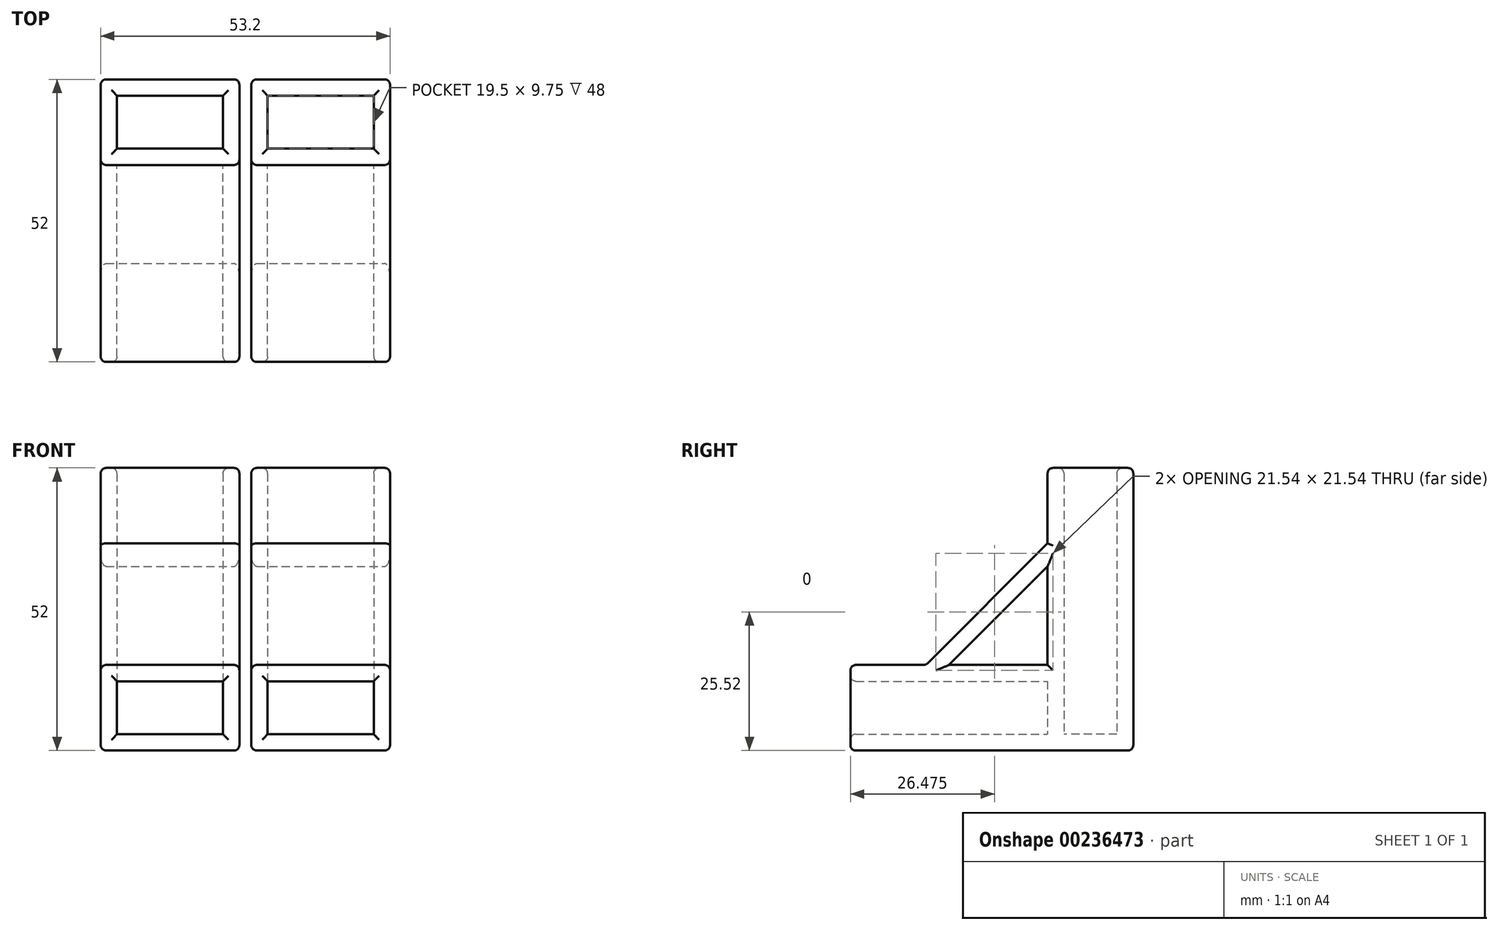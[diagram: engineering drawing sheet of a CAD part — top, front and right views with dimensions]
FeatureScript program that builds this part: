
annotation { "Feature Type Name" : "Feature", "Feature Type Description" : "" }
export const myFeature = defineFeature(function(context is Context, id is Id, definition is map)
    precondition{}
    {
        {
            var Q0;
            Q0=qCreatedBy(makeId("Top.planeOp"),FACE);
            var sketch = newSketch(context, id + "F0", { "sketchPlane" : qUnion([Q0])});
            skLineSegment(sketch, "E0.bottom", {"start": v(-9.75, 4.88) * mm, "end": v(9.75, 4.88) * mm});
            skLineSegment(sketch, "E0.top", {"start": v(-9.75, -4.88) * mm, "end": v(9.75, -4.88) * mm});
            skLineSegment(sketch, "E0.left", {"start": v(-9.75, 4.88) * mm, "end": v(-9.75, -4.88) * mm});
            skLineSegment(sketch, "E0.right", {"start": v(9.75, 4.88) * mm, "end": v(9.75, -4.88) * mm});
            skPoint(sketch, "E0.middle", {"position": v(0, 0) * mm});
            skLineSegment(sketch, "E1.0", {"start": v(-12.75, 7.88) * mm, "end": v(12.75, 7.88) * mm});
            skLineSegment(sketch, "E1.1", {"start": v(-12.75, 7.88) * mm, "end": v(-12.75, -7.88) * mm});
            skLineSegment(sketch, "E1.2", {"start": v(-12.75, -7.88) * mm, "end": v(12.75, -7.88) * mm});
            skLineSegment(sketch, "E1.3", {"start": v(12.75, 7.88) * mm, "end": v(12.75, -7.88) * mm});
            skSolve(sketch);
        }
        {
            var Q0;
            Q0=makeQuery(id+"F0.imprint","IMPRINT",FACE,{"disambiguationData":[TD([[makeQuery(id+"F0.imprint","IMPRINT",EDGE,{"derivedFrom":sQuery(id+"F0.wireOp",EDGE,"E0.bottom")}),1.0]])]});
            extrude(context, id + "F1", {"entities" : qUnion([Q0]), "depth" : 52 * mm, "offsetDistance" : 25 * mm});
        }
        {
            var Q0;
            Q0=makeQuery(id+"F1.opExtrude","SWEPT_FACE",FACE,{"disambiguationData":[OSD([sQuery(id+"F0.wireOp",EDGE,"E1.2")])]});
            var sketch = newSketch(context, id + "F2", { "sketchPlane" : qUnion([Q0])});
            skPoint(sketch, "E2", {"position": v(12.75, 3) * mm});
            skPoint(sketch, "E3", {"position": v(-12.75, 3) * mm});
            skPoint(sketch, "E4", {"position": v(12.75, 12.75) * mm});
            skPoint(sketch, "E5", {"position": v(-12.75, 12.75) * mm});
            skPoint(sketch, "E6", {"position": v(12.75, 15.75) * mm});
            skPoint(sketch, "E7", {"position": v(-12.75, 15.75) * mm});
            skPoint(sketch, "E8", {"position": v(9.75, 0) * mm});
            skPoint(sketch, "E9", {"position": v(9.75, 3) * mm});
            skPoint(sketch, "E10", {"position": v(9.75, 12.75) * mm});
            skPoint(sketch, "E11", {"position": v(9.75, 15.75) * mm});
            skPoint(sketch, "E12", {"position": v(-9.75, 0) * mm});
            skPoint(sketch, "E13", {"position": v(-9.75, 3) * mm});
            skPoint(sketch, "E14", {"position": v(-9.75, 12.75) * mm});
            skPoint(sketch, "E15", {"position": v(-9.75, 15.75) * mm});
            skLineSegment(sketch, "E16", {"start": v(12.75, 15.75) * mm, "end": v(-12.75, 15.75) * mm});
            skLineSegment(sketch, "E17", {"start": v(12.75, 15.75) * mm, "end": v(12.75, 0) * mm});
            skLineSegment(sketch, "E18", {"start": v(12.75, 0) * mm, "end": v(-12.75, 0) * mm});
            skLineSegment(sketch, "E19", {"start": v(-12.75, 0) * mm, "end": v(-12.75, 15.75) * mm});
            skLineSegment(sketch, "E20", {"start": v(9.75, 12.75) * mm, "end": v(9.75, 3) * mm});
            skLineSegment(sketch, "E21", {"start": v(-9.75, 3) * mm, "end": v(9.75, 3) * mm});
            skLineSegment(sketch, "E22", {"start": v(-9.75, 3) * mm, "end": v(-9.75, 12.75) * mm});
            skLineSegment(sketch, "E23", {"start": v(-9.75, 12.75) * mm, "end": v(9.75, 12.75) * mm});
            skSolve(sketch);
        }
        {
            var Q0;
            Q0=makeQuery(id+"F2.imprint","IMPRINT",FACE,{"disambiguationData":[TD([[makeQuery(id+"F2.imprint","IMPRINT",EDGE,{"derivedFrom":sQuery(id+"F2.wireOp",EDGE,"E16")}),1.0]])]});
            extrude(context, id + "F3", {"entities" : qUnion([Q0]), "operationType" : NewBodyOperationType.ADD, "depth" : 36.25 * mm, "offsetDistance" : 25 * mm});
        }
        {
            var Q0;
            Q0=makeQuery(id+"F0.imprint","IMPRINT",FACE,{"disambiguationData":[TD([[makeQuery(id+"F0.imprint","IMPRINT",EDGE,{"derivedFrom":sQuery(id+"F0.wireOp",EDGE,"E0.bottom")}),-1.0]])]});
            extrude(context, id + "F4", {"entities" : qUnion([Q0]), "operationType" : NewBodyOperationType.ADD, "depth" : 3 * mm, "offsetDistance" : 25 * mm});
        }
        {
            var Q0;
            Q0=makeQuery(id+"F3.boolean.opBoolean","MERGE",FACE,{"derivedFrom":[makeQuery(id+"F1.opExtrude","SWEPT_FACE",FACE,{"disambiguationData":[OSD([sQuery(id+"F0.wireOp",EDGE,"E1.3")])]}),makeQuery(id+"F3.opExtrude","SWEPT_FACE",FACE,{"disambiguationData":[OSD([sQuery(id+"F2.wireOp",EDGE,"E17")])]})]});
            var sketch = newSketch(context, id + "F5", { "sketchPlane" : qUnion([Q0])});
            skPoint(sketch, "E24", {"position": v(-26, 15.75) * mm});
            skPoint(sketch, "E25", {"position": v(-7.87, 33.88) * mm});
            skPoint(sketch, "E26", {"position": v(-7.87, 52) * mm});
            skPoint(sketch, "E27", {"position": v(-44.12, 15.75) * mm});
            skLineSegment(sketch, "E28", {"start": v(-7.87, 33.88) * mm, "end": v(-26, 15.75) * mm});
            skPoint(sketch, "E29", {"position": v(-16.94, 24.81) * mm});
            skLineSegment(sketch, "E30.0", {"start": v(-7.87, 38.12) * mm, "end": v(-30.24, 15.75) * mm});
            skSolve(sketch);
        }
        {
            var Q0;
            {var subQ0=sQuery(id+"F5.wireOp",EDGE,"E28");Q0=makeQuery(id+"F5.imprint","IMPRINT",FACE,{"disambiguationData":[TD([[makeQuery(id+"F5.imprint","IMPRINT",EDGE,{"derivedFrom":subQ0}),-1.0]])]});}
            extrude(context, id + "F6", {"entities" : qUnion([Q0]), "operationType" : NewBodyOperationType.ADD, "oppositeDirection" : true, "depth" : 25.5 * mm, "offsetDistance" : 25 * mm});
        }
        {
            var Q0;
            {var subQ0=sQuery(id+"F2.wireOp",EDGE,"E17");var subQ1=sQuery(id+"F0.wireOp",EDGE,"E1.3");Q0=makeQuery(id+"F6.boolean.opBoolean","MERGE",FACE,{"derivedFrom":[makeQuery(id+"F3.boolean.opBoolean","MERGE",FACE,{"derivedFrom":[makeQuery(id+"F1.opExtrude","SWEPT_FACE",FACE,{"disambiguationData":[OSD([subQ1])]}),makeQuery(id+"F3.opExtrude","SWEPT_FACE",FACE,{"disambiguationData":[OSD([subQ0])]})]}),makeQuery(id+"F6.opExtrude","CAP_FACE",FACE,{"disambiguationData":[OSD([sQuery(id+"F0.wireOp",EDGE,"E1.2"),subQ1,sQuery(id+"F2.wireOp",EDGE,"E16"),subQ0,sQuery(id+"F5.wireOp",EDGE,"E28"),sQuery(id+"F5.wireOp",EDGE,"E30.0")])],"isStart":true})]});}
            var Q1;
            {var subQ0=sQuery(id+"F0.wireOp",EDGE,"E0.right");var subQ1=sQuery(id+"F0.wireOp",EDGE,"E0.left");var subQ2=sQuery(id+"F0.wireOp",EDGE,"E0.top");var subQ3=sQuery(id+"F0.wireOp",EDGE,"E0.bottom");Q1=makeQuery(id+"F4.boolean.opBoolean","MERGE",FACE,{"derivedFrom":[makeQuery(id+"F3.boolean.opBoolean","MERGE",FACE,{"derivedFrom":[makeQuery(id+"F1.opExtrude","CAP_FACE",FACE,{"disambiguationData":[OSD([subQ3,subQ2,subQ1,subQ0,sQuery(id+"F0.wireOp",EDGE,"E1.0"),sQuery(id+"F0.wireOp",EDGE,"E1.1"),sQuery(id+"F0.wireOp",EDGE,"E1.2"),sQuery(id+"F0.wireOp",EDGE,"E1.3")])],"isStart":true}),makeQuery(id+"F3.opExtrude","SWEPT_FACE",FACE,{"disambiguationData":[OSD([sQuery(id+"F2.wireOp",EDGE,"E18")])]})]}),makeQuery(id+"F4.opExtrude","CAP_FACE",FACE,{"disambiguationData":[OSD([subQ3,subQ2,subQ1,subQ0])],"isStart":true})]});}
            var Q2;
            Q2=makeQuery(id+"F6.boolean.opBoolean","MERGE",FACE,{"derivedFrom":[makeQuery(id+"F3.boolean.opBoolean","MERGE",FACE,{"derivedFrom":[makeQuery(id+"F1.opExtrude","SWEPT_FACE",FACE,{"disambiguationData":[OSD([sQuery(id+"F0.wireOp",EDGE,"E1.1")])]}),makeQuery(id+"F3.opExtrude","SWEPT_FACE",FACE,{"disambiguationData":[OSD([sQuery(id+"F2.wireOp",EDGE,"E19")])]})]}),makeQuery(id+"F6.opExtrude","CAP_FACE",FACE,{"disambiguationData":[OSD([sQuery(id+"F0.wireOp",EDGE,"E1.2"),sQuery(id+"F0.wireOp",EDGE,"E1.3"),sQuery(id+"F2.wireOp",EDGE,"E16"),sQuery(id+"F2.wireOp",EDGE,"E17"),sQuery(id+"F5.wireOp",EDGE,"E28"),sQuery(id+"F5.wireOp",EDGE,"E30.0")])],"isStart":false})]});
            var Q3;
            Q3=makeQuery(id+"F1.opExtrude","CAP_FACE",FACE,{"disambiguationData":[OSD([sQuery(id+"F0.wireOp",EDGE,"E0.bottom"),sQuery(id+"F0.wireOp",EDGE,"E0.top"),sQuery(id+"F0.wireOp",EDGE,"E0.left"),sQuery(id+"F0.wireOp",EDGE,"E0.right"),sQuery(id+"F0.wireOp",EDGE,"E1.0"),sQuery(id+"F0.wireOp",EDGE,"E1.1"),sQuery(id+"F0.wireOp",EDGE,"E1.2"),sQuery(id+"F0.wireOp",EDGE,"E1.3")])],"isStart":false});
            var Q4;
            {var subQ1=sQuery(id+"F5.wireOp",EDGE,"E30.0");var subQ3=sQuery(id+"F2.wireOp",EDGE,"E16");Q4=makeQuery(id+"F6.boolean.opBoolean","SPLIT",FACE,{"disambiguationData":[TD([makeQuery(id+"F6.opExtrude","SWEPT_FACE",FACE,{"disambiguationData":[OSD([subQ1])]})])],"derivedFrom":makeQuery(id+"F3.opExtrude","SWEPT_FACE",FACE,{"disambiguationData":[OSD([subQ3])]})});}
            var Q5;
            Q5=makeQuery(id+"F3.opExtrude","CAP_FACE",FACE,{"disambiguationData":[OSD([sQuery(id+"F2.wireOp",EDGE,"E16"),sQuery(id+"F2.wireOp",EDGE,"E17"),sQuery(id+"F2.wireOp",EDGE,"E18"),sQuery(id+"F2.wireOp",EDGE,"E19"),sQuery(id+"F2.wireOp",EDGE,"E20"),sQuery(id+"F2.wireOp",EDGE,"E21"),sQuery(id+"F2.wireOp",EDGE,"E22"),sQuery(id+"F2.wireOp",EDGE,"E23")])],"isStart":false});
            fillet(context, id + "F7", {"entities" : qUnion([Q0, Q1, Q2, Q3, Q4, Q5]), "tangentPropagation" : true, "radius" : 1 * mm, "defaultsChanged" : false, "vertexSettings" : [], "allowEdgeOverflow" : false});
        }
        {
            var Q0;
            Q0=makeQuery(id+"F1.opExtrude","SWEPT_BODY",BODY,{"disambiguationData":[OSD([sQuery(id+"F0.wireOp",EDGE,"E0.bottom"),sQuery(id+"F0.wireOp",EDGE,"E0.top"),sQuery(id+"F0.wireOp",EDGE,"E0.left"),sQuery(id+"F0.wireOp",EDGE,"E0.right"),sQuery(id+"F0.wireOp",EDGE,"E1.0"),sQuery(id+"F0.wireOp",EDGE,"E1.1"),sQuery(id+"F0.wireOp",EDGE,"E1.2"),sQuery(id+"F0.wireOp",EDGE,"E1.3")])]});
            transform(context, id + "F8", {"entities" : qUnion([Q0]), "transformType" : TransformType.TRANSLATION_3D, "dx" : 27.7 * mm, "dy" : 0 * mm, "dz" : 0 * mm, "makeCopy" : true});
        }
    });
